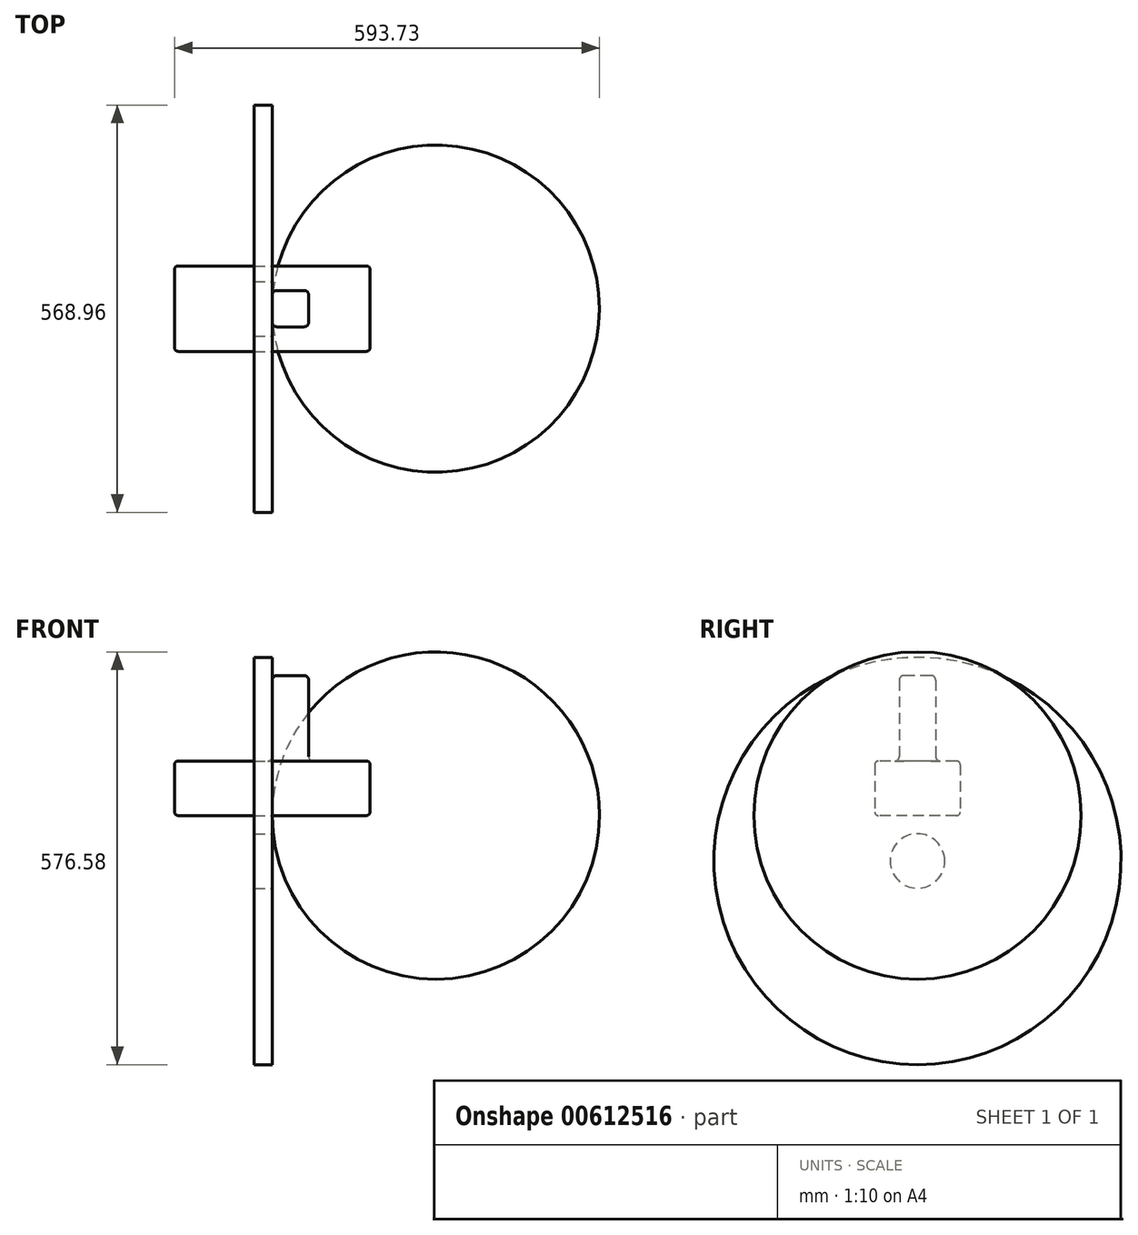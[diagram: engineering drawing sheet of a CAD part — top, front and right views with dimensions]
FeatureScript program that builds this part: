
annotation { "Feature Type Name" : "Feature", "Feature Type Description" : "" }
export const myFeature = defineFeature(function(context is Context, id is Id, definition is map)
    precondition{}
    {
        {
            var Q0;
            Q0=qCreatedBy(makeId("Top.planeOp"),FACE);
            var sketch = newSketch(context, id + "F0", { "sketchPlane" : qUnion([Q0])});
            skLineSegment(sketch, "E0.bottom", {"start": v(-136.53, 59.7) * mm, "end": v(136.53, 59.7) * mm});
            skLineSegment(sketch, "E0.top", {"start": v(-136.53, -59.7) * mm, "end": v(136.53, -59.7) * mm});
            skLineSegment(sketch, "E0.left", {"start": v(-136.53, 59.7) * mm, "end": v(-136.53, -59.7) * mm});
            skLineSegment(sketch, "E0.right", {"start": v(136.53, 59.7) * mm, "end": v(136.53, -59.7) * mm});
            skPoint(sketch, "E1", {"position": v(-136.53, 0) * mm});
            skPoint(sketch, "E2", {"position": v(0, 59.7) * mm});
            skSolve(sketch);
        }
        {
            var Q0;
            Q0=makeQuery(id+"F0.imprint","IMPRINT",FACE,{"disambiguationData":[TD([[makeQuery(id+"F0.imprint","IMPRINT",EDGE,{"derivedFrom":sQuery(id+"F0.wireOp",EDGE,"E0.bottom")}),-1.0]])]});
            extrude(context, id + "F1", {"entities" : qUnion([Q0]), "depth" : 76.2 * mm, "offsetDistance" : 25.4 * mm});
        }
        {
            var Q0;
            Q0=makeQuery(id+"F1.opExtrude","CAP_FACE",FACE,{"disambiguationData":[OSD([sQuery(id+"F0.wireOp",EDGE,"E0.bottom"),sQuery(id+"F0.wireOp",EDGE,"E0.top"),sQuery(id+"F0.wireOp",EDGE,"E0.left"),sQuery(id+"F0.wireOp",EDGE,"E0.right")])],"isStart":false});
            var sketch = newSketch(context, id + "F2", { "sketchPlane" : qUnion([Q0])});
            skLineSegment(sketch, "E3.bottom", {"start": v(0, 25.4) * mm, "end": v(50.8, 25.4) * mm});
            skLineSegment(sketch, "E3.top", {"start": v(0, -25.4) * mm, "end": v(50.8, -25.4) * mm});
            skLineSegment(sketch, "E3.left", {"start": v(0, 25.4) * mm, "end": v(0, -25.4) * mm});
            skLineSegment(sketch, "E3.right", {"start": v(50.8, 25.4) * mm, "end": v(50.8, -25.4) * mm});
            skPoint(sketch, "E4", {"position": v(0, 0) * mm});
            skSolve(sketch);
        }
        {
            var Q0;
            Q0=makeQuery(id+"F2.imprint","IMPRINT",FACE,{"disambiguationData":[TD([[makeQuery(id+"F2.imprint","IMPRINT",EDGE,{"derivedFrom":sQuery(id+"F2.wireOp",EDGE,"E3.bottom")}),-1.0]])]});
            extrude(context, id + "F3", {"entities" : qUnion([Q0]), "operationType" : NewBodyOperationType.ADD, "depth" : 119.38 * mm, "offsetDistance" : 25.4 * mm});
        }
        {
            var Q0;
            Q0=makeQuery(id+"F3.opExtrude","SWEPT_FACE",FACE,{"disambiguationData":[OSD([sQuery(id+"F2.wireOp",EDGE,"E3.left")])]});
            var Q1;
            Q1=makeQuery(id+"F3.opExtrude","SWEPT_FACE",FACE,{"disambiguationData":[OSD([sQuery(id+"F2.wireOp",EDGE,"E3.bottom")])]});
            var Q2;
            Q2=makeQuery(id+"F3.opExtrude","SWEPT_FACE",FACE,{"disambiguationData":[OSD([sQuery(id+"F2.wireOp",EDGE,"E3.right")])]});
            var Q3;
            Q3=makeQuery(id+"F3.opExtrude","SWEPT_FACE",FACE,{"disambiguationData":[OSD([sQuery(id+"F2.wireOp",EDGE,"E3.top")])]});
            fillet(context, id + "F4", {"entities" : qUnion([Q0, Q1, Q2, Q3]), "radius" : 6.35 * mm, "tangentPropagation" : true, "allowEdgeOverflow" : false});
        }
        {
            var Q0;
            Q0=makeQuery(id+"F1.opExtrude","CAP_FACE",FACE,{"disambiguationData":[OSD([sQuery(id+"F0.wireOp",EDGE,"E0.bottom"),sQuery(id+"F0.wireOp",EDGE,"E0.top"),sQuery(id+"F0.wireOp",EDGE,"E0.left"),sQuery(id+"F0.wireOp",EDGE,"E0.right")])],"isStart":false});
            var Q1;
            Q1=makeQuery(id+"F1.opExtrude","CAP_FACE",FACE,{"disambiguationData":[OSD([sQuery(id+"F0.wireOp",EDGE,"E0.bottom"),sQuery(id+"F0.wireOp",EDGE,"E0.top"),sQuery(id+"F0.wireOp",EDGE,"E0.left"),sQuery(id+"F0.wireOp",EDGE,"E0.right")])],"isStart":true});
            var Q2;
            Q2=makeQuery(id+"F1.opExtrude","SWEPT_FACE",FACE,{"disambiguationData":[OSD([sQuery(id+"F0.wireOp",EDGE,"E0.top")])]});
            var Q3;
            Q3=makeQuery(id+"F1.opExtrude","SWEPT_FACE",FACE,{"disambiguationData":[OSD([sQuery(id+"F0.wireOp",EDGE,"E0.bottom")])]});
            fillet(context, id + "F5", {"entities" : qUnion([Q0, Q1, Q2, Q3]), "radius" : 5.08 * mm, "tangentPropagation" : true, "allowEdgeOverflow" : false});
        }
        {
            var Q0;
            Q0=qCreatedBy(makeId("Right.planeOp"),FACE);
            var sketch = newSketch(context, id + "F6", { "sketchPlane" : qUnion([Q0])});
            skLineSegment(sketch, "E5", {"start": v(0, 0) * mm, "end": v(0, -551.53) * mm, "construction": true});
            skCircle(sketch, "E6", {"center": v(0, -63.5) * mm, "radius": 284.48 * mm});
            skCircle(sketch, "E7", {"center": v(0, -63.5) * mm, "radius": 38.1 * mm});
            skSolve(sketch);
        }
        {
            var Q0;
            Q0=makeQuery(id+"F6.imprint","IMPRINT",FACE,{"disambiguationData":[TD([[makeQuery(id+"F6.imprint","IMPRINT",EDGE,{"derivedFrom":sQuery(id+"F6.wireOp",EDGE,"E6")}),1.0]])]});
            extrude(context, id + "F7", {"entities" : qUnion([Q0]), "oppositeDirection" : true, "depth" : 25.4 * mm, "offsetDistance" : 25.4 * mm});
        }
        {
            var Q0;
            Q0=qCreatedBy(makeId("Right.planeOp"),FACE);
            var sketch = newSketch(context, id + "F8", { "sketchPlane" : qUnion([Q0])});
            skCircle(sketch, "E8", {"center": v(0, 0) * mm, "radius": 228.6 * mm});
            skSolve(sketch);
        }
        {
            var Q0;
            Q0=makeQuery(id+"F8.imprint","IMPRINT",FACE,{"disambiguationData":[TD([[makeQuery(id+"F8.imprint","IMPRINT",EDGE,{"derivedFrom":sQuery(id+"F8.wireOp",EDGE,"E8")}),1.0]])]});
            extrude(context, id + "F9", {"entities" : qUnion([Q0]), "depth" : 457.2 * mm, "offsetDistance" : 25.4 * mm});
        }
        {
            var Q0;
            Q0=makeQuery(id+"F9.opExtrude","CAP_FACE",FACE,{"disambiguationData":[OSD([sQuery(id+"F8.wireOp",EDGE,"E8")])],"isStart":false});
            var Q1;
            Q1=makeQuery(id+"F9.opExtrude","CAP_FACE",FACE,{"disambiguationData":[OSD([sQuery(id+"F8.wireOp",EDGE,"E8")])],"isStart":true});
            fillet(context, id + "F10", {"entities" : qUnion([Q0, Q1]), "radius" : 228.6 * mm, "tangentPropagation" : true, "allowEdgeOverflow" : false});
        }
    });
